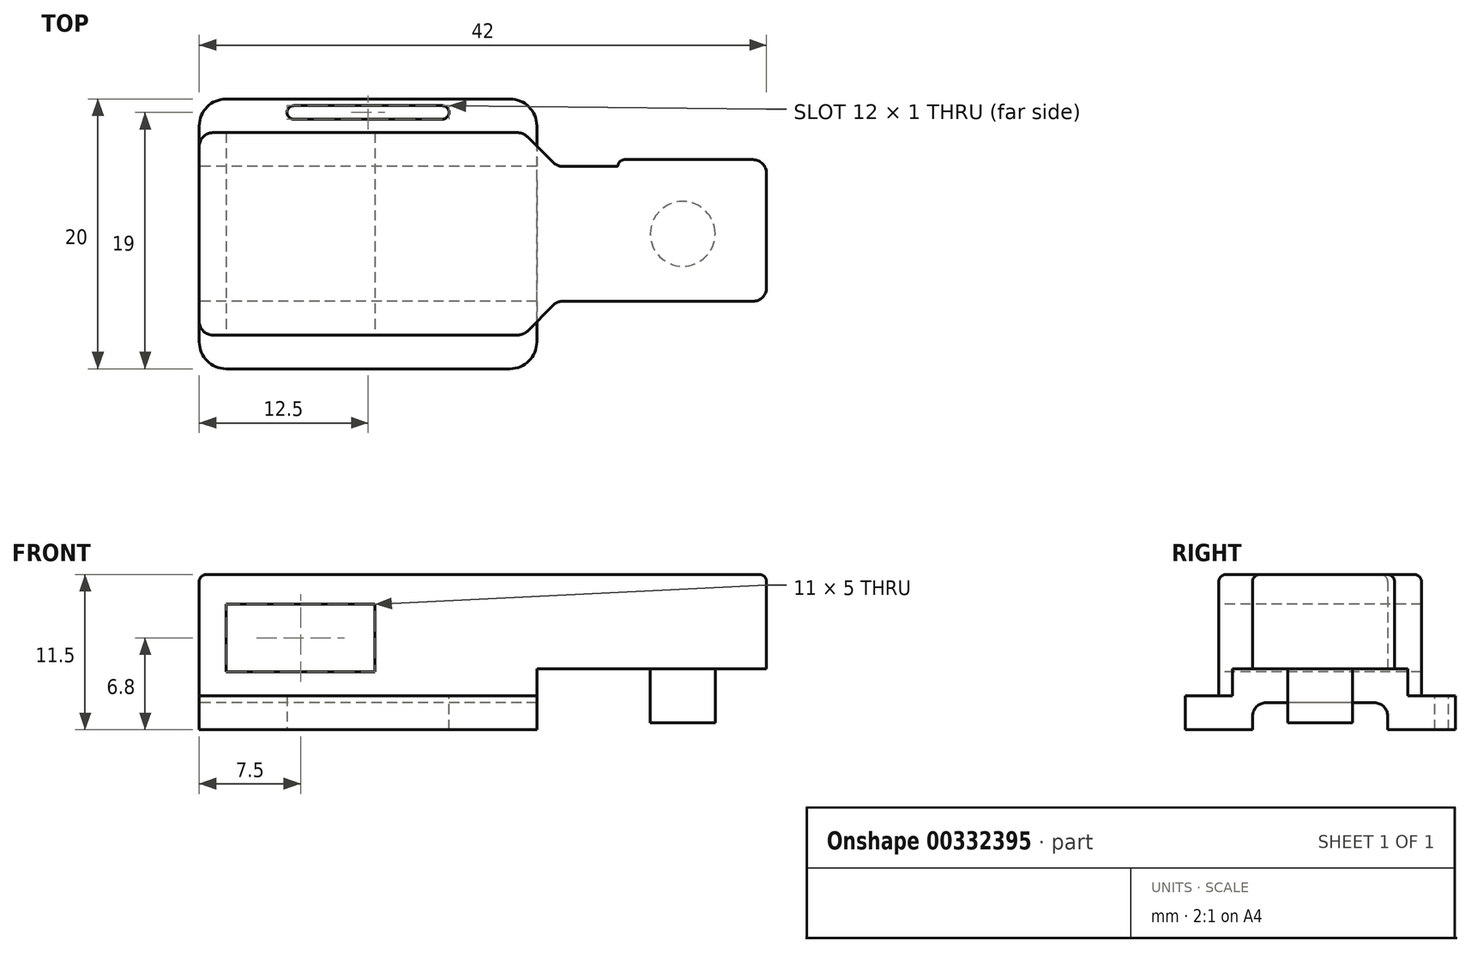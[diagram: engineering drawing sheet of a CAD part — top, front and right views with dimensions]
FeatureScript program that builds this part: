
annotation { "Feature Type Name" : "Feature", "Feature Type Description" : "" }
export const myFeature = defineFeature(function(context is Context, id is Id, definition is map)
    precondition{}
    {
        {
            var Q0;
            Q0=qCreatedBy(makeId("Top.planeOp"),FACE);
            var sketch = newSketch(context, id + "F0", { "sketchPlane" : qUnion([Q0])});
            skLineSegment(sketch, "E0", {"start": v(0, 0) * mm, "end": v(24, 0) * mm});
            skLineSegment(sketch, "E1", {"start": v(24, 0) * mm, "end": v(26.5, 2.5) * mm});
            skLineSegment(sketch, "E2", {"start": v(26.5, 2.5) * mm, "end": v(42, 2.5) * mm});
            skLineSegment(sketch, "E3", {"start": v(42, 2.5) * mm, "end": v(42, 12.5) * mm});
            skLineSegment(sketch, "E4", {"start": v(42, 12.5) * mm, "end": v(26.5, 12.5) * mm});
            skLineSegment(sketch, "E5", {"start": v(26.5, 12.5) * mm, "end": v(24, 15) * mm});
            skLineSegment(sketch, "E6", {"start": v(24, 15) * mm, "end": v(0, 15) * mm});
            skLineSegment(sketch, "E7", {"start": v(0, 15) * mm, "end": v(0, 0) * mm});
            skSolve(sketch);
        }
        {
            var Q0;
            Q0 = qSketchRegion(id + "F0", true);
            extrude(context, id + "F1", {"entities" : qUnion([Q0]), "depth" : 9 * mm});
        }
        {
            var Q0;
            Q0=makeQuery(id+"F1.opExtrude","CAP_FACE",FACE,{"disambiguationData":[OSD([sQuery(id+"F0.wireOp",EDGE,"E0"),sQuery(id+"F0.wireOp",EDGE,"E1"),sQuery(id+"F0.wireOp",EDGE,"E2"),sQuery(id+"F0.wireOp",EDGE,"E3"),sQuery(id+"F0.wireOp",EDGE,"E4"),sQuery(id+"F0.wireOp",EDGE,"E5"),sQuery(id+"F0.wireOp",EDGE,"E6"),sQuery(id+"F0.wireOp",EDGE,"E7")])],"isStart":false});
            var sketch = newSketch(context, id + "F2", { "sketchPlane" : qUnion([Q0])});
            skLineSegment(sketch, "E8.bottom", {"start": v(42, 12.5) * mm, "end": v(31, 12.5) * mm});
            skLineSegment(sketch, "E8.top", {"start": v(42, 13) * mm, "end": v(31, 13) * mm});
            skLineSegment(sketch, "E8.left", {"start": v(42, 12.5) * mm, "end": v(42, 13) * mm});
            skLineSegment(sketch, "E8.right", {"start": v(31, 12.5) * mm, "end": v(31, 13) * mm});
            skSolve(sketch);
        }
        {
            var Q0;
            Q0 = qSketchRegion(id + "F2", true);
            var Q1;
            Q1=makeQuery(id+"F1.opExtrude","CAP_FACE",FACE,{"disambiguationData":[OSD([sQuery(id+"F0.wireOp",EDGE,"E0"),sQuery(id+"F0.wireOp",EDGE,"E1"),sQuery(id+"F0.wireOp",EDGE,"E2"),sQuery(id+"F0.wireOp",EDGE,"E3"),sQuery(id+"F0.wireOp",EDGE,"E4"),sQuery(id+"F0.wireOp",EDGE,"E5"),sQuery(id+"F0.wireOp",EDGE,"E6"),sQuery(id+"F0.wireOp",EDGE,"E7")])],"isStart":true});
            extrude(context, id + "F3", {"entities" : qUnion([Q0]), "operationType" : NewBodyOperationType.ADD, "endBound" : BoundingType.UP_TO_SURFACE, "oppositeDirection" : true, "endBoundEntityFace" : qUnion([Q1]), "depth" : 25 * mm});
        }
        {
            var Q0;
            {var subQ0=sQuery(id+"F0.wireOp",EDGE,"E7");var subQ1=sQuery(id+"F0.wireOp",EDGE,"E6");var subQ2=sQuery(id+"F0.wireOp",EDGE,"E5");var subQ3=sQuery(id+"F0.wireOp",EDGE,"E4");var subQ4=sQuery(id+"F0.wireOp",EDGE,"E3");var subQ5=sQuery(id+"F0.wireOp",EDGE,"E2");var subQ6=sQuery(id+"F0.wireOp",EDGE,"E1");var subQ7=sQuery(id+"F0.wireOp",EDGE,"E0");Q0=makeQuery(id+"F3.boolean.opBoolean","MERGE",FACE,{"derivedFrom":[makeQuery(id+"F1.opExtrude","CAP_FACE",FACE,{"disambiguationData":[OSD([subQ7,subQ6,subQ5,subQ4,subQ3,subQ2,subQ1,subQ0])],"isStart":true}),makeQuery(id+"F3.opExtrude","CAP_FACE",FACE,{"disambiguationData":[OSD([subQ7,subQ6,subQ5,subQ4,subQ3,subQ2,subQ1,subQ0])],"isStart":false})]});}
            var sketch = newSketch(context, id + "F4", { "sketchPlane" : qUnion([Q0])});
            skLineSegment(sketch, "E9.bottom", {"start": v(42, 2.5) * mm, "end": v(25, 2.5) * mm});
            skLineSegment(sketch, "E9.top", {"start": v(42, -18.87) * mm, "end": v(25, -18.87) * mm});
            skLineSegment(sketch, "E9.left", {"start": v(42, 2.5) * mm, "end": v(42, -18.87) * mm});
            skLineSegment(sketch, "E9.right", {"start": v(25, 2.5) * mm, "end": v(25, -18.87) * mm});
            skSolve(sketch);
        }
        {
            var Q0;
            Q0 = qSketchRegion(id + "F4", true);
            extrude(context, id + "F5", {"entities" : qUnion([Q0]), "operationType" : NewBodyOperationType.REMOVE, "oppositeDirection" : true, "depth" : 2 * mm});
        }
        {
            var Q0;
            {var subQ0=sQuery(id+"F0.wireOp",EDGE,"E7");var subQ1=sQuery(id+"F0.wireOp",EDGE,"E6");var subQ2=sQuery(id+"F0.wireOp",EDGE,"E5");var subQ3=sQuery(id+"F0.wireOp",EDGE,"E4");var subQ4=sQuery(id+"F0.wireOp",EDGE,"E3");var subQ5=sQuery(id+"F0.wireOp",EDGE,"E2");var subQ6=sQuery(id+"F0.wireOp",EDGE,"E1");var subQ7=sQuery(id+"F0.wireOp",EDGE,"E0");Q0=makeQuery(id+"F3.boolean.opBoolean","MERGE",FACE,{"derivedFrom":[makeQuery(id+"F1.opExtrude","CAP_FACE",FACE,{"disambiguationData":[OSD([subQ7,subQ6,subQ5,subQ4,subQ3,subQ2,subQ1,subQ0])],"isStart":true}),makeQuery(id+"F3.opExtrude","CAP_FACE",FACE,{"disambiguationData":[OSD([subQ7,subQ6,subQ5,subQ4,subQ3,subQ2,subQ1,subQ0])],"isStart":false})]});}
            var sketch = newSketch(context, id + "F6", { "sketchPlane" : qUnion([Q0])});
            skLineSegment(sketch, "E10.bottom", {"start": v(25, -17.5) * mm, "end": v(0, -17.5) * mm});
            skLineSegment(sketch, "E10.top", {"start": v(25, 2.5) * mm, "end": v(0, 2.5) * mm});
            skLineSegment(sketch, "E10.left", {"start": v(25, -17.5) * mm, "end": v(25, 2.5) * mm});
            skLineSegment(sketch, "E10.right", {"start": v(0, -17.5) * mm, "end": v(0, 2.5) * mm});
            skSolve(sketch);
        }
        {
            var Q0;
            Q0 = qSketchRegion(id + "F6", true);
            extrude(context, id + "F7", {"entities" : qUnion([Q0]), "operationType" : NewBodyOperationType.ADD, "depth" : 2.5 * mm});
        }
        {
            var Q0;
            Q0=makeQuery(id+"F7.boolean.opBoolean","MERGE",FACE,{"derivedFrom":[makeQuery(id+"F1.opExtrude","SWEPT_FACE",FACE,{"disambiguationData":[OSD([sQuery(id+"F0.wireOp",EDGE,"E7")])]}),makeQuery(id+"F7.opExtrude","SWEPT_FACE",FACE,{"disambiguationData":[OSD([sQuery(id+"F6.wireOp",EDGE,"E10.right")])]})]});
            var sketch = newSketch(context, id + "F8", { "sketchPlane" : qUnion([Q0])});
            skLineSegment(sketch, "E11.bottom", {"start": v(-12.5, -2.5) * mm, "end": v(-2.5, -2.5) * mm});
            skLineSegment(sketch, "E11.top", {"start": v(-12.5, -0.5) * mm, "end": v(-2.5, -0.5) * mm});
            skLineSegment(sketch, "E11.left", {"start": v(-12.5, -2.5) * mm, "end": v(-12.5, -0.5) * mm});
            skLineSegment(sketch, "E11.right", {"start": v(-2.5, -2.5) * mm, "end": v(-2.5, -0.5) * mm});
            skSolve(sketch);
        }
        {
            var Q0;
            Q0 = qSketchRegion(id + "F8", true);
            extrude(context, id + "F9", {"entities" : qUnion([Q0]), "operationType" : NewBodyOperationType.REMOVE, "endBound" : BoundingType.THROUGH_ALL, "oppositeDirection" : true, "depth" : 25 * mm});
        }
        {
            var Q0;
            Q0=makeQuery(id+"F1.opExtrude","SWEPT_FACE",FACE,{"disambiguationData":[OSD([sQuery(id+"F0.wireOp",EDGE,"E0")])]});
            var sketch = newSketch(context, id + "F10", { "sketchPlane" : qUnion([Q0])});
            skLineSegment(sketch, "E12.bottom", {"start": v(2, 6.8) * mm, "end": v(13, 6.8) * mm});
            skLineSegment(sketch, "E12.top", {"start": v(2, 1.8) * mm, "end": v(13, 1.8) * mm});
            skLineSegment(sketch, "E12.left", {"start": v(2, 6.8) * mm, "end": v(2, 1.8) * mm});
            skLineSegment(sketch, "E12.right", {"start": v(13, 6.8) * mm, "end": v(13, 1.8) * mm});
            skSolve(sketch);
        }
        {
            var Q0;
            Q0 = qSketchRegion(id + "F10", true);
            extrude(context, id + "F11", {"entities" : qUnion([Q0]), "operationType" : NewBodyOperationType.REMOVE, "oppositeDirection" : true, "depth" : 25 * mm});
        }
        {
            var Q0;
            Q0=makeQuery(id+"F5.boolean.opBoolean","COPY",FACE,{"derivedFrom":makeQuery(id+"F5.opExtrude","CAP_FACE",FACE,{"disambiguationData":[OSD([sQuery(id+"F4.wireOp",EDGE,"E9.bottom"),sQuery(id+"F4.wireOp",EDGE,"E9.top"),sQuery(id+"F4.wireOp",EDGE,"E9.left"),sQuery(id+"F4.wireOp",EDGE,"E9.right")])],"isStart":false})});
            var sketch = newSketch(context, id + "F12", { "sketchPlane" : qUnion([Q0])});
            skCircle(sketch, "E13", {"center": v(35.8, -7.5) * mm, "radius": 2.4 * mm});
            skPoint(sketch, "E13.centerSnap0", {"position": v(25, -7.5) * mm});
            skSolve(sketch);
        }
        {
            var Q0;
            Q0 = qSketchRegion(id + "F12", true);
            extrude(context, id + "F13", {"entities" : qUnion([Q0]), "operationType" : NewBodyOperationType.ADD, "depth" : 4 * mm});
        }
        {
            var Q0;
            Q0=makeQuery(id+"F1.opExtrude","SWEPT_EDGE",EDGE,{"disambiguationData":[OSD([sQuery(id+"F0.wireOp",EDGE,"E1"),sQuery(id+"F0.wireOp",EDGE,"E2")])]});
            var Q1;
            Q1=makeQuery(id+"F1.opExtrude","SWEPT_EDGE",EDGE,{"disambiguationData":[OSD([sQuery(id+"F0.wireOp",EDGE,"E0"),sQuery(id+"F0.wireOp",EDGE,"E1")])]});
            var Q2;
            Q2=makeQuery(id+"F1.opExtrude","SWEPT_EDGE",EDGE,{"disambiguationData":[OSD([sQuery(id+"F0.wireOp",EDGE,"E5"),sQuery(id+"F0.wireOp",EDGE,"E6")])]});
            var Q3;
            Q3=makeQuery(id+"F1.opExtrude","SWEPT_EDGE",EDGE,{"disambiguationData":[OSD([sQuery(id+"F0.wireOp",EDGE,"E4"),sQuery(id+"F0.wireOp",EDGE,"E5")])]});
            var Q4;
            Q4=makeQuery(id+"F3.opExtrude","SWEPT_EDGE",EDGE,{"disambiguationData":[OSD([sQuery(id+"F2.wireOp",EDGE,"E8.top"),sQuery(id+"F2.wireOp",EDGE,"E8.left")])]});
            var Q5;
            Q5=makeQuery(id+"F1.opExtrude","SWEPT_EDGE",EDGE,{"disambiguationData":[OSD([sQuery(id+"F0.wireOp",EDGE,"E2"),sQuery(id+"F0.wireOp",EDGE,"E3")])]});
            var Q6;
            Q6=makeQuery(id+"F1.opExtrude","SWEPT_EDGE",EDGE,{"disambiguationData":[OSD([sQuery(id+"F0.wireOp",EDGE,"E6"),sQuery(id+"F0.wireOp",EDGE,"E7")])]});
            var Q7;
            Q7=makeQuery(id+"F1.opExtrude","SWEPT_EDGE",EDGE,{"disambiguationData":[OSD([sQuery(id+"F0.wireOp",EDGE,"E0"),sQuery(id+"F0.wireOp",EDGE,"E7")])]});
            fillet(context, id + "F14", {"entities" : qUnion([Q0, Q1, Q2, Q3, Q4, Q5, Q6, Q7]), "radius" : 1 * mm, "tangentPropagation" : true, "allowEdgeOverflow" : false});
        }
        {
            var Q0;
            Q0=makeQuery(id+"F3.opExtrude","SWEPT_EDGE",EDGE,{"disambiguationData":[OSD([sQuery(id+"F2.wireOp",EDGE,"E8.top"),sQuery(id+"F2.wireOp",EDGE,"E8.right")])]});
            fillet(context, id + "F15", {"entities" : qUnion([Q0]), "radius" : 0.5 * mm, "tangentPropagation" : true, "allowEdgeOverflow" : false});
        }
        {
            var Q0;
            Q0=makeQuery(id+"F9.boolean.opBoolean","COPY",EDGE,{"derivedFrom":makeQuery(id+"F9.opExtrude","SWEPT_EDGE",EDGE,{"disambiguationData":[OSD([sQuery(id+"F8.wireOp",EDGE,"E11.top"),sQuery(id+"F8.wireOp",EDGE,"E11.right")])]})});
            var Q1;
            Q1=makeQuery(id+"F9.boolean.opBoolean","COPY",EDGE,{"derivedFrom":makeQuery(id+"F9.opExtrude","SWEPT_EDGE",EDGE,{"disambiguationData":[OSD([sQuery(id+"F8.wireOp",EDGE,"E11.top"),sQuery(id+"F8.wireOp",EDGE,"E11.left")])]})});
            fillet(context, id + "F16", {"entities" : qUnion([Q0, Q1]), "radius" : 1 * mm, "tangentPropagation" : true, "allowEdgeOverflow" : false});
        }
        {
            var Q0;
            Q0=makeQuery(id+"F7.opExtrude","SWEPT_EDGE",EDGE,{"disambiguationData":[OSD([sQuery(id+"F6.wireOp",EDGE,"E10.top"),sQuery(id+"F6.wireOp",EDGE,"E10.left")])]});
            var Q1;
            Q1=makeQuery(id+"F7.opExtrude","SWEPT_EDGE",EDGE,{"disambiguationData":[OSD([sQuery(id+"F6.wireOp",EDGE,"E10.top"),sQuery(id+"F6.wireOp",EDGE,"E10.right")])]});
            var Q2;
            Q2=makeQuery(id+"F7.opExtrude","SWEPT_EDGE",EDGE,{"disambiguationData":[OSD([sQuery(id+"F6.wireOp",EDGE,"E10.bottom"),sQuery(id+"F6.wireOp",EDGE,"E10.right")])]});
            var Q3;
            Q3=makeQuery(id+"F7.opExtrude","SWEPT_EDGE",EDGE,{"disambiguationData":[OSD([sQuery(id+"F6.wireOp",EDGE,"E10.bottom"),sQuery(id+"F6.wireOp",EDGE,"E10.left")])]});
            fillet(context, id + "F17", {"entities" : qUnion([Q0, Q1, Q2, Q3]), "radius" : 2 * mm, "tangentPropagation" : true, "allowEdgeOverflow" : false});
        }
        {
            var Q0;
            Q0=makeQuery(id+"F15.opFillet","BLEND_EDGE",EDGE,{"blendedFrom":[makeQuery(id+"F3.opExtrude","SWEPT_EDGE",EDGE,{"disambiguationData":[OSD([sQuery(id+"F2.wireOp",EDGE,"E8.top"),sQuery(id+"F2.wireOp",EDGE,"E8.right")])]}),makeQuery(id+"F1.opExtrude","SWEPT_FACE",FACE,{"disambiguationData":[OSD([sQuery(id+"F0.wireOp",EDGE,"E4")])]})],"blendedInto":[makeQuery(id+"F1.opExtrude","SWEPT_FACE",FACE,{"disambiguationData":[OSD([sQuery(id+"F0.wireOp",EDGE,"E4")])]})]});
            fillet(context, id + "F18", {"entities" : qUnion([Q0]), "radius" : 0.1 * mm, "tangentPropagation" : true, "allowEdgeOverflow" : false});
        }
        {
            var Q0;
            Q0=makeQuery(id+"F3.boolean.opBoolean","MERGE",FACE,{"derivedFrom":[makeQuery(id+"F1.opExtrude","CAP_FACE",FACE,{"disambiguationData":[OSD([sQuery(id+"F0.wireOp",EDGE,"E0"),sQuery(id+"F0.wireOp",EDGE,"E1"),sQuery(id+"F0.wireOp",EDGE,"E2"),sQuery(id+"F0.wireOp",EDGE,"E3"),sQuery(id+"F0.wireOp",EDGE,"E4"),sQuery(id+"F0.wireOp",EDGE,"E5"),sQuery(id+"F0.wireOp",EDGE,"E6"),sQuery(id+"F0.wireOp",EDGE,"E7")])],"isStart":false}),makeQuery(id+"F3.opExtrude","CAP_FACE",FACE,{"disambiguationData":[OSD([sQuery(id+"F2.wireOp",EDGE,"E8.bottom"),sQuery(id+"F2.wireOp",EDGE,"E8.top"),sQuery(id+"F2.wireOp",EDGE,"E8.left"),sQuery(id+"F2.wireOp",EDGE,"E8.right")])],"isStart":true})]});
            fillet(context, id + "F19", {"entities" : qUnion([Q0]), "radius" : 0.5 * mm, "tangentPropagation" : true, "allowEdgeOverflow" : false});
        }
        {
            var Q0;
            {var subQ0=sQuery(id+"F6.wireOp",EDGE,"E10.right");var subQ1=sQuery(id+"F6.wireOp",EDGE,"E10.left");var subQ2=sQuery(id+"F6.wireOp",EDGE,"E10.bottom");Q0=makeQuery(id+"F7.boolean.opBoolean","SPLIT",FACE,{"disambiguationData":[TD([makeQuery(id+"F1.opExtrude","SWEPT_FACE",FACE,{"disambiguationData":[OSD([sQuery(id+"F0.wireOp",EDGE,"E5")])]})])],"derivedFrom":makeQuery(id+"F7.opExtrude","CAP_FACE",FACE,{"disambiguationData":[OSD([subQ2,sQuery(id+"F6.wireOp",EDGE,"E10.top"),subQ1,subQ0])],"isStart":true})});}
            var sketch = newSketch(context, id + "F20", { "sketchPlane" : qUnion([Q0])});
            skLineSegment(sketch, "E14.bottom", {"start": v(6.5, 16) * mm, "end": v(18.5, 16) * mm});
            skLineSegment(sketch, "E14.top", {"start": v(6.5, 17) * mm, "end": v(18.5, 17) * mm});
            skLineSegment(sketch, "E14.left", {"start": v(6.5, 16) * mm, "end": v(6.5, 17) * mm});
            skLineSegment(sketch, "E14.right", {"start": v(18.5, 16) * mm, "end": v(18.5, 17) * mm});
            skSolve(sketch);
        }
        {
            var Q0;
            Q0 = qSketchRegion(id + "F20", true);
            extrude(context, id + "F21", {"entities" : qUnion([Q0]), "operationType" : NewBodyOperationType.REMOVE, "oppositeDirection" : true, "depth" : 25 * mm});
        }
        {
            var Q0;
            Q0=makeQuery(id+"F21.boolean.opBoolean","COPY",EDGE,{"derivedFrom":makeQuery(id+"F21.opExtrude","SWEPT_EDGE",EDGE,{"disambiguationData":[OSD([sQuery(id+"F20.wireOp",EDGE,"E14.top"),sQuery(id+"F20.wireOp",EDGE,"E14.left")])]})});
            var Q1;
            Q1=makeQuery(id+"F21.boolean.opBoolean","COPY",EDGE,{"derivedFrom":makeQuery(id+"F21.opExtrude","SWEPT_EDGE",EDGE,{"disambiguationData":[OSD([sQuery(id+"F20.wireOp",EDGE,"E14.bottom"),sQuery(id+"F20.wireOp",EDGE,"E14.left")])]})});
            var Q2;
            Q2=makeQuery(id+"F21.boolean.opBoolean","COPY",EDGE,{"derivedFrom":makeQuery(id+"F21.opExtrude","SWEPT_EDGE",EDGE,{"disambiguationData":[OSD([sQuery(id+"F20.wireOp",EDGE,"E14.top"),sQuery(id+"F20.wireOp",EDGE,"E14.right")])]})});
            var Q3;
            Q3=makeQuery(id+"F21.boolean.opBoolean","COPY",EDGE,{"derivedFrom":makeQuery(id+"F21.opExtrude","SWEPT_EDGE",EDGE,{"disambiguationData":[OSD([sQuery(id+"F20.wireOp",EDGE,"E14.bottom"),sQuery(id+"F20.wireOp",EDGE,"E14.right")])]})});
            fillet(context, id + "F22", {"entities" : qUnion([Q0, Q1, Q2, Q3]), "radius" : 0.5 * mm, "tangentPropagation" : true, "allowEdgeOverflow" : false});
        }
        {
            var Q0;
            Q0=makeQuery(id+"F5.boolean.opBoolean","COPY",EDGE,{"derivedFrom":makeQuery(id+"F5.opExtrude","CAP_EDGE",EDGE,{"disambiguationData":[OSD([sQuery(id+"F4.wireOp",EDGE,"E9.right")])],"isStart":false})});
            cPoint(context, id + "F23", {"entities" : qUnion([Q0]), "parameter" : 0.5});
        }
        {
            var Q0;
            Q0=makeQuery(id+"F1.opExtrude","SWEPT_FACE",FACE,{"disambiguationData":[OSD([sQuery(id+"F0.wireOp",EDGE,"E0")])]});
            var Q1;
            Q1 = qCreatedBy(id + "F23" ,VERTEX);
            cPlane(context, id + "F24", {"entities" : qUnion([Q0, Q1]), "cplaneType" : CPlaneType.PLANE_POINT, "offset" : 25 * mm, "width" : 150 * mm, "height" : 150 * mm});
        }
    });
